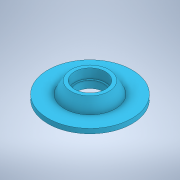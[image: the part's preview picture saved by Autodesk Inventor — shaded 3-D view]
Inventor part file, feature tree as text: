
AUTODESK INVENTOR PART (.ipt)
format: ipt  version: 2022.2 (Build 262287000, 287)  size: 123,392 bytes
history: native  units: mm
features: revolve x1, sketch x1
ambient origin geometry x8: Origin, YZ Plane, XZ Plane, XY Plane, X Axis, Y Axis, Z Axis, Center Point
bodies: Solid1 (feature_tree)
feature tree (2):
  revolve  "Revolution1"  [1 undecoded]
  sketch  "Sketch2"  dims[d0=13.0mm d1=1.5mm d2=3.0mm d3=24.0mm d4=6.0mm d5=8.0mm d6=0.0mm d7=4.0mm d8=14.0mm d9=90.0deg]
note: 1 required parameter value undecoded (feature->parameter linkage not recoverable at this tier; creation-order binding heuristic only, values carry confidence <= 0.55)
